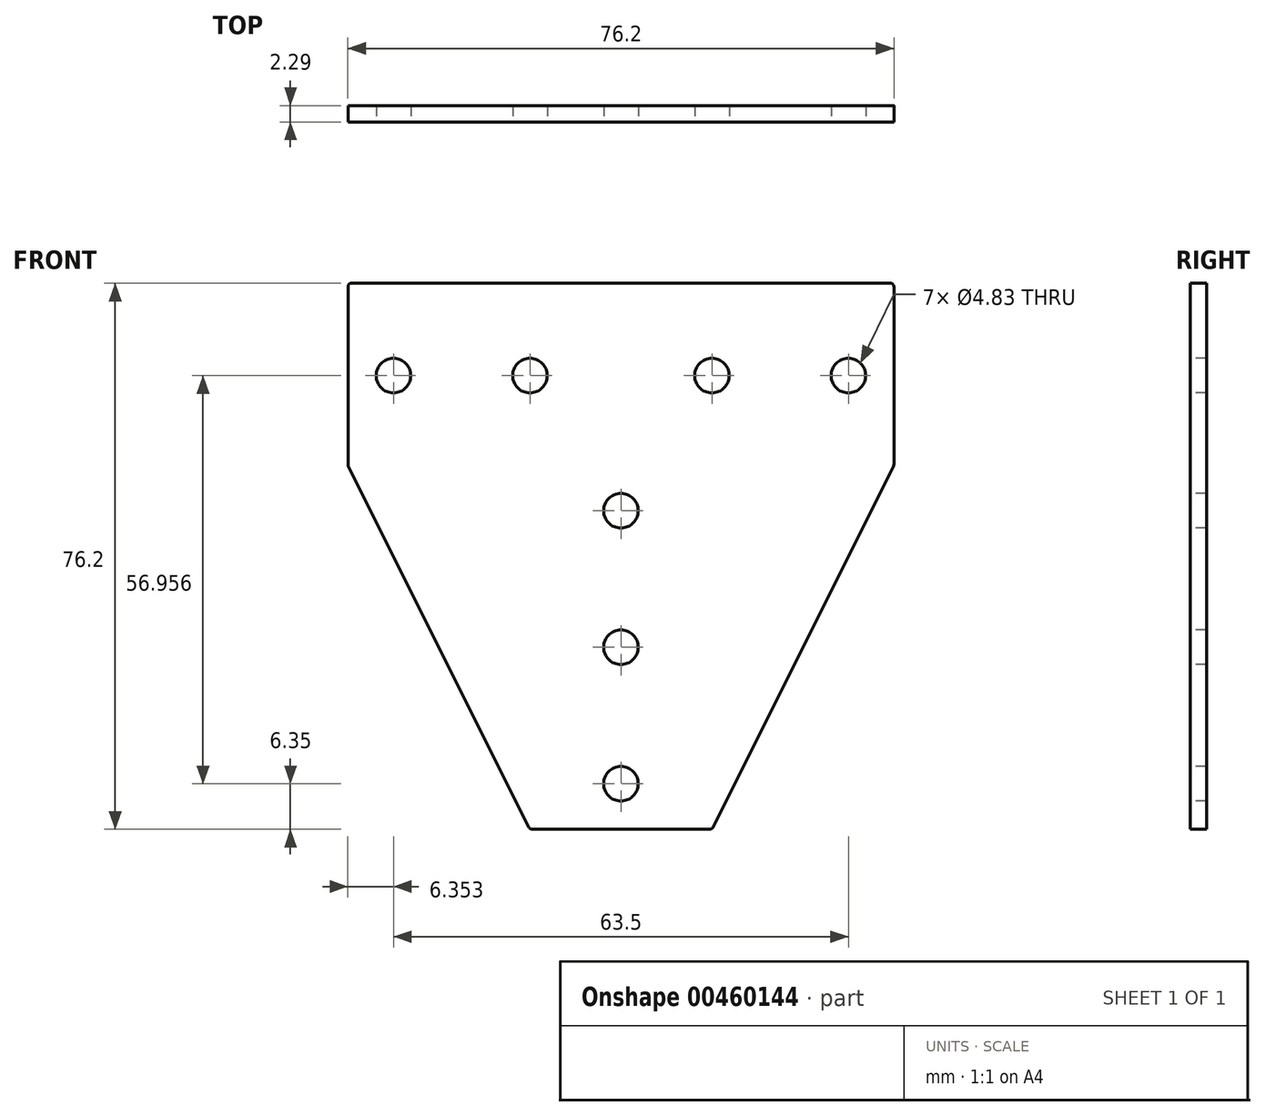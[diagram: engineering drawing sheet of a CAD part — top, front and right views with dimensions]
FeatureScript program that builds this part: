
annotation { "Feature Type Name" : "Feature", "Feature Type Description" : "" }
export const myFeature = defineFeature(function(context is Context, id is Id, definition is map)
    precondition{}
    {
        {
            var Q0;
            Q0=qCreatedBy(makeId("Front.planeOp"),FACE);
            var sketch = newSketch(context, id + "F0", { "sketchPlane" : qUnion([Q0])});
            skLineSegment(sketch, "E0", {"start": v(-37.07, 0) * mm, "end": v(39.13, 0) * mm});
            skLineSegment(sketch, "E1", {"start": v(39.13, 0) * mm, "end": v(39.13, -25.4) * mm});
            skLineSegment(sketch, "E2", {"start": v(39.13, -25.4) * mm, "end": v(13.73, -76.2) * mm});
            skLineSegment(sketch, "E3", {"start": v(13.73, -76.2) * mm, "end": v(-11.67, -76.2) * mm});
            skLineSegment(sketch, "E4", {"start": v(-37.07, 0) * mm, "end": v(-37.07, -25.4) * mm});
            skLineSegment(sketch, "E5", {"start": v(-37.07, -25.4) * mm, "end": v(-11.67, -76.2) * mm});
            skSolve(sketch);
        }
        {
            var Q0;
            Q0=makeQuery(id+"F0.imprint","IMPRINT",FACE,{"disambiguationData":[TD([[makeQuery(id+"F0.imprint","IMPRINT",EDGE,{"derivedFrom":sQuery(id+"F0.wireOp",EDGE,"E0")}),-1.0]])]});
            extrude(context, id + "F1", {"entities" : qUnion([Q0]), "depth" : 2.3 * mm});
        }
        {
            var Q0;
            Q0=makeQuery(id+"F1.opExtrude","SWEPT_EDGE",EDGE,{"disambiguationData":[OSD([sQuery(id+"F0.wireOp",EDGE,"E0"),sQuery(id+"F0.wireOp",EDGE,"E4")])]});
            var Q1;
            Q1=makeQuery(id+"F1.opExtrude","SWEPT_EDGE",EDGE,{"disambiguationData":[OSD([sQuery(id+"F0.wireOp",EDGE,"E4"),sQuery(id+"F0.wireOp",EDGE,"E5")])]});
            var Q2;
            Q2=makeQuery(id+"F1.opExtrude","SWEPT_EDGE",EDGE,{"disambiguationData":[OSD([sQuery(id+"F0.wireOp",EDGE,"E0"),sQuery(id+"F0.wireOp",EDGE,"E1")])]});
            var Q3;
            Q3=makeQuery(id+"F1.opExtrude","SWEPT_EDGE",EDGE,{"disambiguationData":[OSD([sQuery(id+"F0.wireOp",EDGE,"E1"),sQuery(id+"F0.wireOp",EDGE,"E2")])]});
            var Q4;
            Q4=makeQuery(id+"F1.opExtrude","SWEPT_EDGE",EDGE,{"disambiguationData":[OSD([sQuery(id+"F0.wireOp",EDGE,"E2"),sQuery(id+"F0.wireOp",EDGE,"E3")])]});
            var Q5;
            Q5=makeQuery(id+"F1.opExtrude","SWEPT_EDGE",EDGE,{"disambiguationData":[OSD([sQuery(id+"F0.wireOp",EDGE,"E3"),sQuery(id+"F0.wireOp",EDGE,"E5")])]});
            fillet(context, id + "F2", {"entities" : qUnion([Q0, Q1, Q2, Q3, Q4, Q5]), "radius" : 0.5 * mm, "tangentPropagation" : true, "allowEdgeOverflow" : false});
        }
        {
            var Q0;
            Q0=makeQuery(id+"F1.opExtrude","CAP_FACE",FACE,{"disambiguationData":[OSD([sQuery(id+"F0.wireOp",EDGE,"E0"),sQuery(id+"F0.wireOp",EDGE,"E1"),sQuery(id+"F0.wireOp",EDGE,"E2"),sQuery(id+"F0.wireOp",EDGE,"E3"),sQuery(id+"F0.wireOp",EDGE,"E4"),sQuery(id+"F0.wireOp",EDGE,"E5")])],"isStart":false});
            var sketch = newSketch(context, id + "F3", { "sketchPlane" : qUnion([Q0])});
            skLineSegment(sketch, "E6", {"start": v(1.03, -76.2) * mm, "end": v(1.03, 0) * mm, "construction": true});
            skLineSegment(sketch, "E7", {"start": v(-37.07, -12.9) * mm, "end": v(39.13, -12.9) * mm, "construction": true});
            skCircle(sketch, "E8", {"center": v(1.03, -69.85) * mm, "radius": 2.41 * mm});
            skCircle(sketch, "E9", {"center": v(1.03, -50.8) * mm, "radius": 2.41 * mm});
            skCircle(sketch, "E10", {"center": v(1.03, -31.75) * mm, "radius": 2.41 * mm});
            skCircle(sketch, "E11", {"center": v(-30.72, -12.9) * mm, "radius": 2.41 * mm});
            skCircle(sketch, "E12", {"center": v(-11.67, -12.9) * mm, "radius": 2.41 * mm});
            skCircle(sketch, "E13", {"center": v(13.73, -12.9) * mm, "radius": 2.41 * mm});
            skCircle(sketch, "E14", {"center": v(32.78, -12.9) * mm, "radius": 2.41 * mm});
            skSolve(sketch);
        }
        {
            var Q0;
            Q0=makeQuery(id+"F3.imprint","IMPRINT",FACE,{"disambiguationData":[TD([[makeQuery(id+"F3.imprint","IMPRINT",EDGE,{"derivedFrom":sQuery(id+"F3.wireOp",EDGE,"E11")}),1.0]])]});
            var Q1;
            Q1=makeQuery(id+"F3.imprint","IMPRINT",FACE,{"disambiguationData":[TD([[makeQuery(id+"F3.imprint","IMPRINT",EDGE,{"derivedFrom":sQuery(id+"F3.wireOp",EDGE,"E12")}),1.0]])]});
            var Q2;
            Q2=makeQuery(id+"F3.imprint","IMPRINT",FACE,{"disambiguationData":[TD([[makeQuery(id+"F3.imprint","IMPRINT",EDGE,{"derivedFrom":sQuery(id+"F3.wireOp",EDGE,"E13")}),1.0]])]});
            var Q3;
            Q3=makeQuery(id+"F3.imprint","IMPRINT",FACE,{"disambiguationData":[TD([[makeQuery(id+"F3.imprint","IMPRINT",EDGE,{"derivedFrom":sQuery(id+"F3.wireOp",EDGE,"E14")}),1.0]])]});
            var Q4;
            Q4=makeQuery(id+"F3.imprint","IMPRINT",FACE,{"disambiguationData":[TD([[makeQuery(id+"F3.imprint","IMPRINT",EDGE,{"derivedFrom":sQuery(id+"F3.wireOp",EDGE,"E10")}),1.0]])]});
            var Q5;
            Q5=makeQuery(id+"F3.imprint","IMPRINT",FACE,{"disambiguationData":[TD([[makeQuery(id+"F3.imprint","IMPRINT",EDGE,{"derivedFrom":sQuery(id+"F3.wireOp",EDGE,"E9")}),1.0]])]});
            var Q6;
            Q6=makeQuery(id+"F3.imprint","IMPRINT",FACE,{"disambiguationData":[TD([[makeQuery(id+"F3.imprint","IMPRINT",EDGE,{"derivedFrom":sQuery(id+"F3.wireOp",EDGE,"E8")}),1.0]])]});
            extrude(context, id + "F4", {"entities" : qUnion([Q0, Q1, Q2, Q3, Q4, Q5, Q6]), "operationType" : NewBodyOperationType.REMOVE, "oppositeDirection" : true, "depth" : 2.3 * mm});
        }
    });
